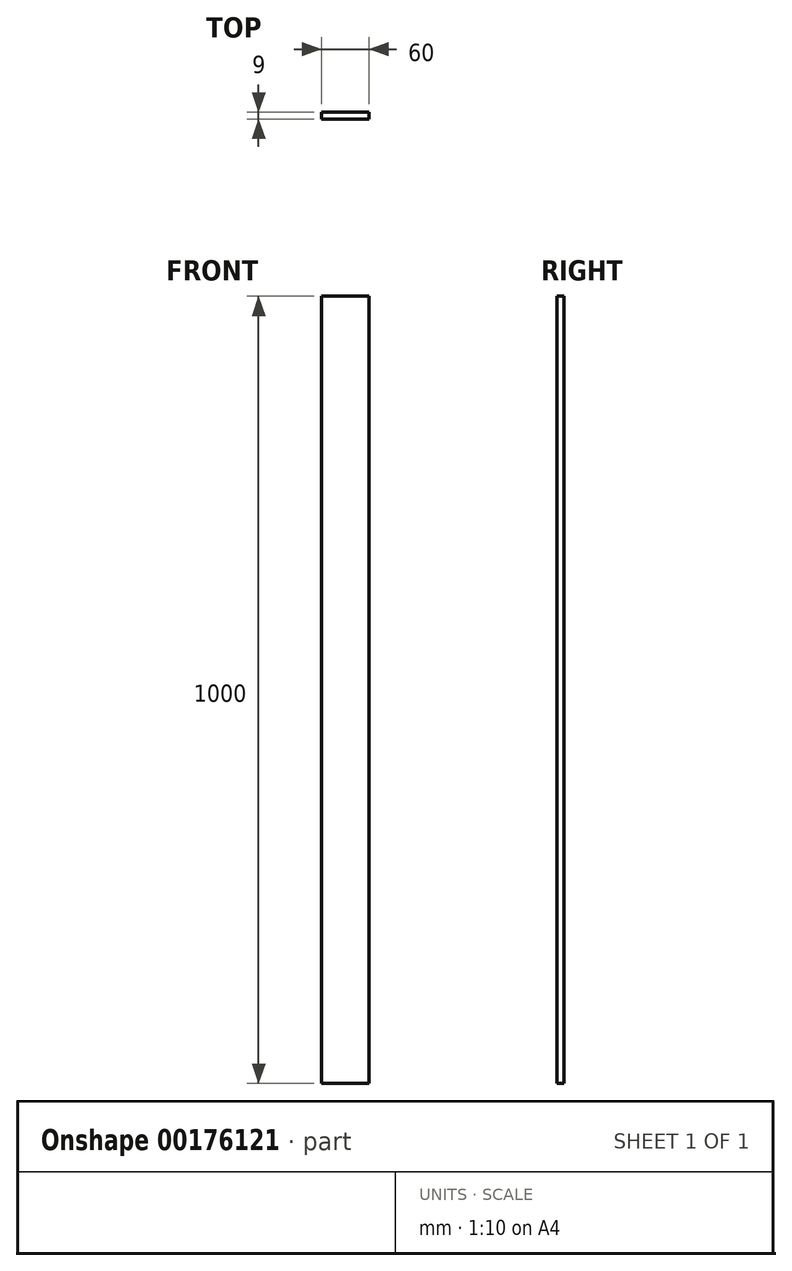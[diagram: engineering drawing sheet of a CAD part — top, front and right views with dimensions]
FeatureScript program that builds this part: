
annotation { "Feature Type Name" : "Feature", "Feature Type Description" : "" }
export const myFeature = defineFeature(function(context is Context, id is Id, definition is map)
    precondition{}
    {
        {
            var Q0;
            Q0=qCreatedBy(makeId("Front.planeOp"),FACE);
            var sketch = newSketch(context, id + "F0", { "sketchPlane" : qUnion([Q0])});
            skLineSegment(sketch, "E0.bottom", {"start": v(0, 0) * mm, "end": v(60, 0) * mm});
            skLineSegment(sketch, "E0.top", {"start": v(0, 1000) * mm, "end": v(60, 1000) * mm});
            skLineSegment(sketch, "E0.left", {"start": v(0, 0) * mm, "end": v(0, 1000) * mm});
            skLineSegment(sketch, "E0.right", {"start": v(60, 0) * mm, "end": v(60, 1000) * mm});
            skSolve(sketch);
        }
        {
            var Q0;
            Q0 = qSketchRegion(id + "F0", true);
            extrude(context, id + "F1", {"entities" : qUnion([Q0]), "depth" : 9 * mm});
        }
    });
